FCSTD DOCUMENT  (FreeCAD 0.19R24291 (Git))
Label: strainer3
License: All rights reserved
LicenseURL: http://en.wikipedia.org/wiki/All_rights_reserved
objects: Sketcher::SketchObject×3, PartDesign::Pocket×2, PartDesign::PolarPattern×2, PartDesign::Fillet×2, PartDesign::Revolution×1, PartDesign::Body×1
note: 16 computed .brp shape members not serialized (recipe doc carries the construction recipe); baked Part::Feature solids carry a one-line shape summary decoded from their .brp

FEATURE [Sketcher::SketchObject] Sketch
  FullyConstrained = true
  MapMode = 5
  Placement = pos=(0,0,0) rot=(1,0,0;1.5708rad)
  Support = -> [XZ_Plane]
  sketch-geometry (10):
    g0: LineSegment StartX=50 StartY=0 StartZ=0 EndX=40 EndY=0 EndZ=0
    g1: LineSegment StartX=40 StartY=0 StartZ=0 EndX=23 EndY=-28 EndZ=0
    g2: LineSegment StartX=23 StartY=-28 StartZ=0 EndX=19.6444 EndY=-28 EndZ=0
    g3: LineSegment StartX=19.6444 StartY=-28 StartZ=0 EndX=12 EndY=15 EndZ=0
    g4: LineSegment StartX=12 StartY=15 StartZ=0 EndX=10 EndY=15 EndZ=0
    g5: LineSegment StartX=10 StartY=15 StartZ=0 EndX=18 EndY=-30 EndZ=0
    g6: LineSegment StartX=18 StartY=-30 StartZ=0 EndX=25 EndY=-30 EndZ=0
    g7: LineSegment StartX=25 StartY=-30 StartZ=0 EndX=42 EndY=-2 EndZ=0
    g8: LineSegment StartX=42 StartY=-2 StartZ=0 EndX=62 EndY=-2 EndZ=0
    g9: LineSegment StartX=50 StartY=0 StartZ=0 EndX=62 EndY=-2 EndZ=0
  constraints (30):
    c: PointOnObject(g0,g-1)
    c: Horizontal(g0)
    c: Coincident(g0,g1)
    c: Coincident(g1,g2)
    c: Coincident(g2,g3)
    c: Coincident(g3,g4)
    c: Horizontal(g4)
    c: Coincident(g4,g5)
    c: Coincident(g5,g6)
    c: Coincident(g6,g7)
    c: Coincident(g7,g8)
    c: Horizontal(g8)
    c: Coincident(g9,g0)
    c: Coincident(g9,g8)
    c: Horizontal(g2)
    c: Horizontal(g6)
    c: Parallel(g3,g5)
    c: DistanceY(g6,g1) = 2
    c: DistanceY(g8,g0) = 2
    c: DistanceX(g4,g4) = 2
    c: DistanceY(g5,g-1) = 30
    c: DistanceY(g-1,g4) = 15
    c: DistanceX(g-1,g0) = 40
    c: DistanceX(g0,g0) = 10
    c: Parallel(g7,g1)
    c: DistanceX(g7,g8) = 20
    c: DistanceX(g4) = 10
    c: DistanceX(g0,g7) = 2
    c: DistanceX(g6,g7) = 17
    c: DistanceX(g4,g5) = 8
FEATURE [PartDesign::Revolution] Revolution
  Angle = 360
  Axis = (0,-2e-16,1)
  Base = (0,0,0)
  Placement = pos=(0,0,0) rot=(1,0,0;1.5708rad)
  Profile = -> Sketch
  ReferenceAxis = -> Sketch [V_Axis]
  Refine = true
  Reversed = true
FEATURE [Sketcher::SketchObject] Sketch001
  FullyConstrained = true
  MapMode = 5
  Placement = pos=(0,0,0) rot=(1,0,0;1.5708rad)
  Support = -> [XZ_Plane]
  sketch-geometry (6):
    g0: Circle CenterX=0 CenterY=-6 CenterZ=0 NormalX=0 NormalY=0 NormalZ=1 AngleXU=0 Radius=2
    g1: Circle CenterX=0 CenterY=-12 CenterZ=0 NormalX=0 NormalY=0 NormalZ=1 AngleXU=0 Radius=2
    g2: Circle CenterX=0 CenterY=-18 CenterZ=0 NormalX=0 NormalY=0 NormalZ=1 AngleXU=0 Radius=2
    g3: Circle CenterX=0 CenterY=-24 CenterZ=0 NormalX=0 NormalY=0 NormalZ=1 AngleXU=0 Radius=2
    g4: Circle CenterX=0 CenterY=3 CenterZ=0 NormalX=0 NormalY=0 NormalZ=1 AngleXU=0 Radius=2
    g5: Circle CenterX=0 CenterY=9 CenterZ=0 NormalX=0 NormalY=0 NormalZ=1 AngleXU=0 Radius=2
  constraints (18):
    c: PointOnObject(g0,g-2)
    c: Radius(g0) = 2
    c: DistanceY(g0,g-1) = 6
    c: PointOnObject(g1,g-2)
    c: DistanceY(g1,g0) = 6
    c: Radius(g1) = 2
    c: PointOnObject(g2,g-2)
    c: PointOnObject(g3,g-2)
    c: Radius(g2) = 2
    c: Radius(g3) = 2
    c: DistanceY(g2,g1) = 6
    c: DistanceY(g3,g2) = 6
    c: PointOnObject(g4,g-2)
    c: Radius(g4) = 2
    c: DistanceY(g-1,g4) = 3
    c: PointOnObject(g5,g-2)
    c: Radius(g5) = 2
    c: DistanceY(g4,g5) = 6
FEATURE [PartDesign::Pocket] Pocket
  BaseFeature = -> Revolution
  Length = 5
  Length2 = 100
  Placement = pos=(0,0,0) rot=(1,0,0;1.5708rad)
  Profile = -> Sketch001
  Refine = true
  Type = 1
FEATURE [PartDesign::PolarPattern] PolarPattern
  Angle = 360
  Axis = -> Z_Axis
  BaseFeature = -> Pocket
  Occurrences = 12
  Originals = -> [Pocket]
  Placement = pos=(0,0,0) rot=(1,0,0;1.5708rad)
  Refine = true
FEATURE [Sketcher::SketchObject] Sketch002
  FullyConstrained = false
  MapMode = 5
  Support = -> [XY_Plane]
  sketch-geometry (3):
    g0: Circle CenterX=6.47048 CenterY=-24.1481 CenterZ=0 NormalX=0 NormalY=0 NormalZ=1 AngleXU=0 Radius=2
    g1: Circle CenterX=8.02339 CenterY=-29.9437 CenterZ=0 NormalX=0 NormalY=0 NormalZ=1 AngleXU=0 Radius=2
    g2: LineSegment StartX=0 StartY=0 StartZ=0 EndX=11.6115 EndY=-43.3346 EndZ=0
  constraints (8):
    c: Radius(g0) = 2
    c: Radius(g1) = 2
    c: Coincident(g2,g-1)
    c: Angle(g2,g-2) = 2.87979
    c: PointOnObject(g0,g2)
    c: PointOnObject(g1,g2)
    c: Distance(g0,g1) = 6
    c: Distance(g-1,g0) = 25
FEATURE [PartDesign::Pocket] Pocket001
  BaseFeature = -> PolarPattern
  Length = 5
  Length2 = 100
  Placement = pos=(0,0,0) rot=(1,0,0;1.5708rad)
  Profile = -> Sketch002
  Refine = true
  Type = 1
FEATURE [PartDesign::PolarPattern] PolarPattern001
  Angle = 360
  Axis = -> Z_Axis
  BaseFeature = -> Pocket001
  Occurrences = 12
  Originals = -> [Pocket001]
  Placement = pos=(0,0,0) rot=(1,0,0;1.5708rad)
  Refine = true
FEATURE [PartDesign::Fillet] Fillet001
  Base = -> PolarPattern001 [Edge330]
  BaseFeature = -> PolarPattern001
  Placement = pos=(0,0,0) rot=(1,0,0;1.5708rad)
  Radius = 1
  Refine = true
  SupportTransform = false
FEATURE [PartDesign::Fillet] Fillet002
  Base = -> Fillet001 [Edge337]
  BaseFeature = -> Fillet001
  Placement = pos=(0,0,0) rot=(1,0,0;1.5708rad)
  Radius = 1
  Refine = true
  SupportTransform = false
FEATURE [PartDesign::Body] Body
  Group = -> [Sketch,Revolution,Sketch001,Pocket,PolarPattern,Sketch002,Pocket001,PolarPattern001,Fillet001,Fillet002]
  Origin = -> Origin
  Tip = -> Fillet002
